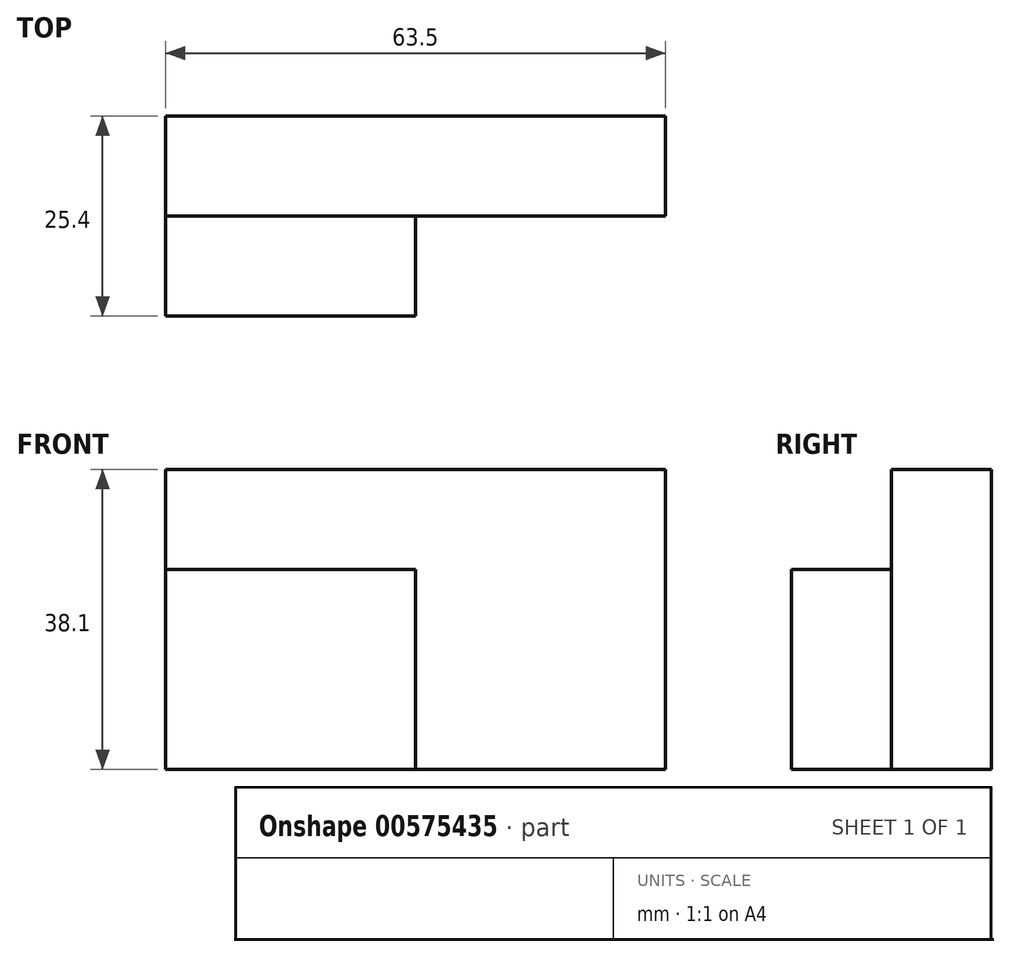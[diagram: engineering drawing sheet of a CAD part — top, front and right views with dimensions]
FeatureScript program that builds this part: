
annotation { "Feature Type Name" : "Feature", "Feature Type Description" : "" }
export const myFeature = defineFeature(function(context is Context, id is Id, definition is map)
    precondition{}
    {
        {
            var Q0;
            Q0=qCreatedBy(makeId("Top.planeOp"),FACE);
            var sketch = newSketch(context, id + "F0", { "sketchPlane" : qUnion([Q0])});
            skLineSegment(sketch, "E0.bottom", {"start": v(0, 0) * mm, "end": v(63.5, 0) * mm});
            skLineSegment(sketch, "E0.top", {"start": v(0, -12.7) * mm, "end": v(31.75, -12.7) * mm});
            skLineSegment(sketch, "E0.left", {"start": v(0, 0) * mm, "end": v(0, -12.7) * mm});
            skLineSegment(sketch, "E0.right", {"start": v(63.5, 0) * mm, "end": v(63.5, -12.7) * mm});
            skLineSegment(sketch, "E1.bottom", {"start": v(0, -12.7) * mm, "end": v(0, -12.7) * mm});
            skLineSegment(sketch, "E1.top", {"start": v(0, -25.4) * mm, "end": v(31.75, -25.4) * mm});
            skLineSegment(sketch, "E1.left", {"start": v(0, -12.7) * mm, "end": v(0, -25.4) * mm});
            skLineSegment(sketch, "E1.right", {"start": v(31.75, -12.7) * mm, "end": v(31.75, -25.4) * mm});
            skLineSegment(sketch, "E2", {"start": v(31.75, -12.7) * mm, "end": v(63.5, -12.7) * mm});
            skSolve(sketch);
        }
        {
            var Q0;
            Q0=makeQuery(id+"F0.imprint","IMPRINT",FACE,{"disambiguationData":[TD([[makeQuery(id+"F0.imprint","IMPRINT",EDGE,{"derivedFrom":sQuery(id+"F0.wireOp",EDGE,"E0.bottom")}),-1.0]])]});
            extrude(context, id + "F1", {"entities" : qUnion([Q0]), "depth" : 38.1 * mm, "offsetDistance" : 25.4 * mm});
        }
        {
            var Q0;
            Q0 = qSketchRegion(id + "F0", true);
            extrude(context, id + "F2", {"entities" : qUnion([Q0]), "operationType" : NewBodyOperationType.ADD, "depth" : 25.4 * mm, "offsetDistance" : 25.4 * mm});
        }
    });
